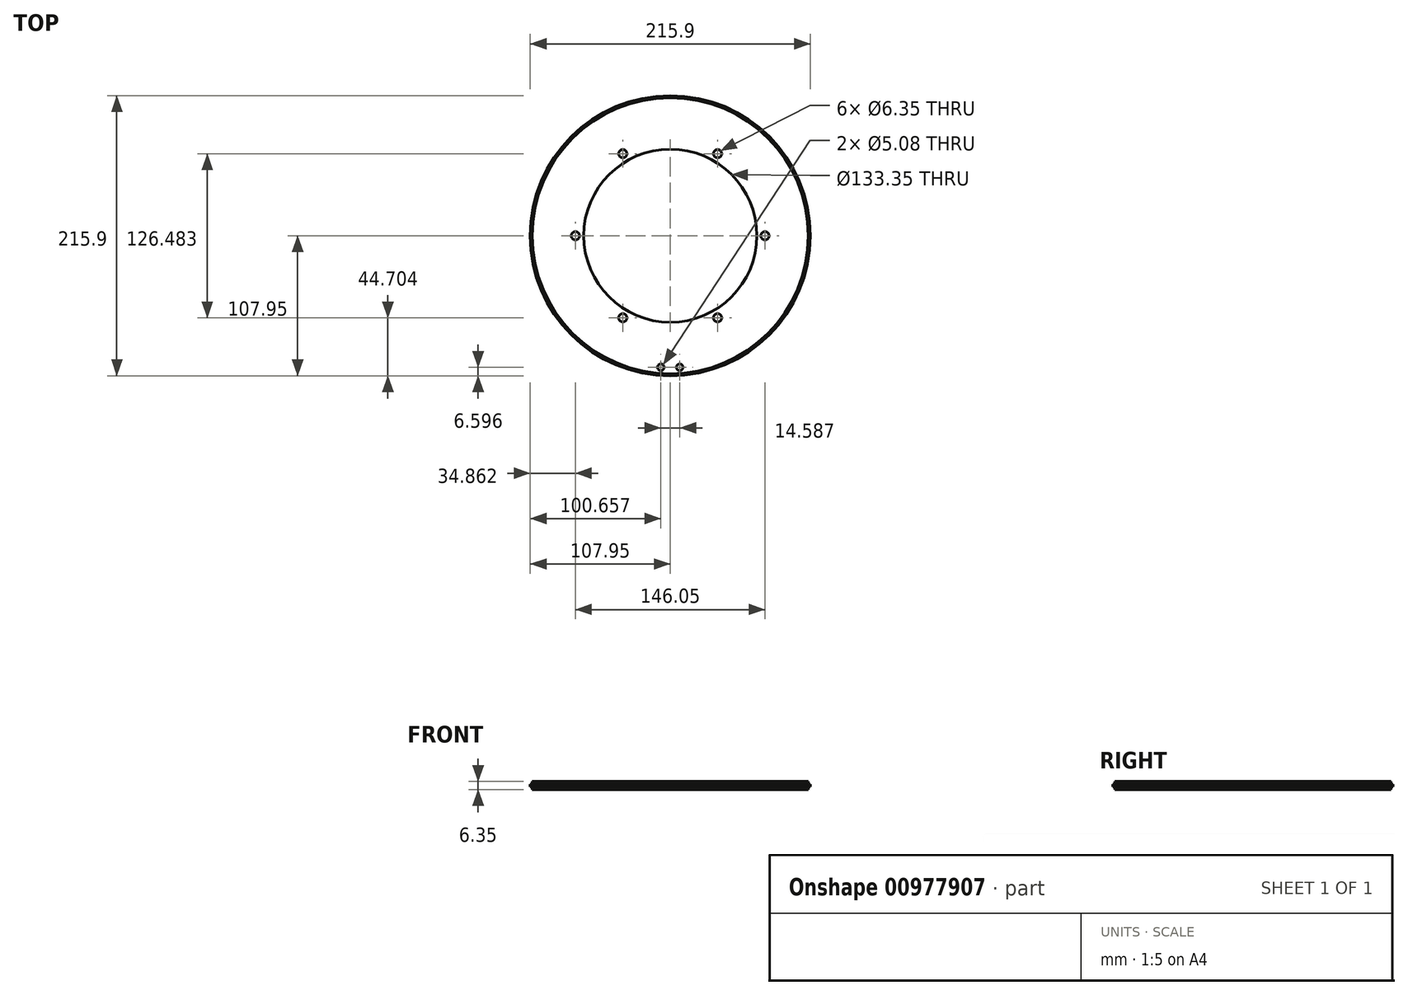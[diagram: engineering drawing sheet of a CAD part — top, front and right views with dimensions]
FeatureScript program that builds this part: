
annotation { "Feature Type Name" : "Feature", "Feature Type Description" : "" }
export const myFeature = defineFeature(function(context is Context, id is Id, definition is map)
    precondition{}
    {
        {
            var Q0;
            Q0=qCreatedBy(makeId("Top.planeOp"),FACE);
            var sketch = newSketch(context, id + "F0", { "sketchPlane" : qUnion([Q0])});
            skCircle(sketch, "E0", {"center": v(0, 0) * mm, "radius": 107.95 * mm});
            skCircle(sketch, "E1", {"center": v(0, 0) * mm, "radius": 106.35 * mm});
            skSolve(sketch);
        }
        {
            var Q0;
            Q0=makeQuery(id+"F0.imprint","IMPRINT",FACE,{"disambiguationData":[TD([[makeQuery(id+"F0.imprint","IMPRINT",EDGE,{"derivedFrom":sQuery(id+"F0.wireOp",EDGE,"E1")}),1.0]])]});
            extrude(context, id + "F1", {"entities" : qUnion([Q0]), "depth" : 2.12 * mm, "offsetDistance" : 25.4 * mm});
        }
        {
            var Q0;
            Q0 = qSketchRegion(id + "F0", true);
            var Q1;
            Q1=makeQuery(id+"F1.opExtrude","CAP_FACE",FACE,{"disambiguationData":[OSD([sQuery(id+"F0.wireOp",EDGE,"E1")])],"isStart":true});
            extrude(context, id + "F2", {"entities" : qUnion([Q0, Q1]), "operationType" : NewBodyOperationType.ADD, "oppositeDirection" : true, "depth" : 2.12 * mm, "offsetDistance" : 25.4 * mm});
        }
        {
            var Q0;
            Q0=makeQuery(id+"F0.imprint","IMPRINT",FACE,{"disambiguationData":[TD([[makeQuery(id+"F0.imprint","IMPRINT",EDGE,{"derivedFrom":sQuery(id+"F0.wireOp",EDGE,"E1")}),1.0]])]});
            extrude(context, id + "F3", {"entities" : qUnion([Q0]), "operationType" : NewBodyOperationType.ADD, "oppositeDirection" : true, "depth" : 4.23 * mm, "offsetDistance" : 25.4 * mm});
        }
        {
            var Q0;
            Q0=makeQuery(id+"F1.opExtrude","CAP_FACE",FACE,{"disambiguationData":[OSD([sQuery(id+"F0.wireOp",EDGE,"E1")])],"isStart":false});
            var sketch = newSketch(context, id + "F4", { "sketchPlane" : qUnion([Q0])});
            skCircle(sketch, "E2", {"center": v(0, 0) * mm, "radius": 66.68 * mm});
            skSolve(sketch);
        }
        {
            var Q0;
            Q0 = qSketchRegion(id + "F4", true);
            extrude(context, id + "F5", {"entities" : qUnion([Q0]), "operationType" : NewBodyOperationType.REMOVE, "endBound" : BoundingType.THROUGH_ALL, "oppositeDirection" : true, "depth" : 25.4 * mm, "offsetDistance" : 25.4 * mm});
        }
        {
            var Q0;
            Q0=makeQuery(id+"F1.opExtrude","CAP_FACE",FACE,{"disambiguationData":[OSD([sQuery(id+"F0.wireOp",EDGE,"E1")])],"isStart":false});
            var sketch = newSketch(context, id + "F6", { "sketchPlane" : qUnion([Q0])});
            skCircle(sketch, "E3", {"center": v(-0.06, 0) * mm, "radius": 79.4 * mm});
            skCircle(sketch, "E4", {"center": v(-0.06, 0) * mm, "radius": 77.76 * mm});
            skCircle(sketch, "E5.0", {"center": v(-73.09, 0) * mm, "radius": 3.17 * mm});
            skCircle(sketch, "E6.0", {"center": v(-36.58, 63.24) * mm, "radius": 3.17 * mm});
            skCircle(sketch, "E7.0", {"center": v(36.45, 63.24) * mm, "radius": 3.17 * mm});
            skCircle(sketch, "E8.0", {"center": v(72.96, 0) * mm, "radius": 3.17 * mm});
            skCircle(sketch, "E9.0", {"center": v(36.45, -63.25) * mm, "radius": 3.17 * mm});
            skCircle(sketch, "E10.0", {"center": v(-36.58, -63.25) * mm, "radius": 3.17 * mm});
            skCircle(sketch, "E11.0", {"center": v(-7.36, -72.66) * mm, "radius": 2.54 * mm});
            skCircle(sketch, "E12.0", {"center": v(7.23, -72.66) * mm, "radius": 2.54 * mm});
            skCircle(sketch, "E13.0", {"center": v(-0.06, 0) * mm, "radius": 66.67 * mm});
            skSolve(sketch);
        }
        {
            var Q0;
            Q0=makeQuery(id+"F6.imprint","IMPRINT",FACE,{"disambiguationData":[TD([[makeQuery(id+"F6.imprint","IMPRINT",EDGE,{"derivedFrom":sQuery(id+"F6.wireOp",EDGE,"E5.0")}),1.0]])]});
            var Q1;
            Q1=makeQuery(id+"F6.imprint","IMPRINT",FACE,{"disambiguationData":[TD([[makeQuery(id+"F6.imprint","IMPRINT",EDGE,{"derivedFrom":sQuery(id+"F6.wireOp",EDGE,"E7.0")}),1.0]])]});
            var Q2;
            Q2=makeQuery(id+"F6.imprint","IMPRINT",FACE,{"disambiguationData":[TD([[makeQuery(id+"F6.imprint","IMPRINT",EDGE,{"derivedFrom":sQuery(id+"F6.wireOp",EDGE,"E8.0")}),1.0]])]});
            var Q3;
            Q3=makeQuery(id+"F6.imprint","IMPRINT",FACE,{"disambiguationData":[TD([[makeQuery(id+"F6.imprint","IMPRINT",EDGE,{"derivedFrom":sQuery(id+"F6.wireOp",EDGE,"E9.0")}),1.0]])]});
            var Q4;
            Q4=makeQuery(id+"F6.imprint","IMPRINT",FACE,{"disambiguationData":[TD([[makeQuery(id+"F6.imprint","IMPRINT",EDGE,{"derivedFrom":sQuery(id+"F6.wireOp",EDGE,"E10.0")}),1.0]])]});
            var Q5;
            Q5=makeQuery(id+"F6.imprint","IMPRINT",FACE,{"disambiguationData":[TD([[makeQuery(id+"F6.imprint","IMPRINT",EDGE,{"derivedFrom":sQuery(id+"F6.wireOp",EDGE,"E6.0")}),1.0]])]});
            extrude(context, id + "F7", {"entities" : qUnion([Q0, Q1, Q2, Q3, Q4, Q5]), "operationType" : NewBodyOperationType.REMOVE, "oppositeDirection" : true, "depth" : 25.4 * mm, "offsetDistance" : 25.4 * mm});
        }
        {
            var Q0;
            Q0=makeQuery(id+"F1.opExtrude","CAP_FACE",FACE,{"disambiguationData":[OSD([sQuery(id+"F0.wireOp",EDGE,"E1")])],"isStart":false});
            var sketch = newSketch(context, id + "F8", { "sketchPlane" : qUnion([Q0])});
            skCircle(sketch, "E14", {"center": v(-7.3, -101.35) * mm, "radius": 2.54 * mm});
            skCircle(sketch, "E15", {"center": v(7.3, -101.35) * mm, "radius": 2.54 * mm});
            skLineSegment(sketch, "E16", {"start": v(0, 0) * mm, "end": v(0, -109.25) * mm});
            skSolve(sketch);
        }
        {
            var Q0;
            Q0=makeQuery(id+"F8.imprint","IMPRINT",FACE,{"disambiguationData":[TD([[makeQuery(id+"F8.imprint","IMPRINT",EDGE,{"derivedFrom":sQuery(id+"F8.wireOp",EDGE,"E14")}),1.0]])]});
            var Q1;
            Q1=makeQuery(id+"F8.imprint","IMPRINT",FACE,{"disambiguationData":[TD([[makeQuery(id+"F8.imprint","IMPRINT",EDGE,{"derivedFrom":sQuery(id+"F8.wireOp",EDGE,"E15")}),1.0]])]});
            extrude(context, id + "F9", {"entities" : qUnion([Q0, Q1]), "operationType" : NewBodyOperationType.REMOVE, "endBound" : BoundingType.THROUGH_ALL, "oppositeDirection" : true, "depth" : 25.4 * mm, "offsetDistance" : 25.4 * mm});
        }
    });
